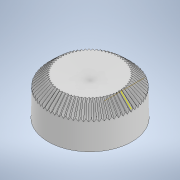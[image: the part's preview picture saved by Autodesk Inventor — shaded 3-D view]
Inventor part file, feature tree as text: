
AUTODESK INVENTOR PART (.ipt)
format: ipt  version: 2022 (Build 260153000, 153)  size: 1,119,232 bytes
history: native  units: mm
features: sketch x5, extrude x3, revolve x1, plane x1, pattern_circular x1, shell x1, fillet x1, projected_geometry x1
ambient origin geometry x8: Origin, YZ Plane, XZ Plane, XY Plane, X Axis, Y Axis, Z Axis, Center Point
bodies: Solid1 (feature_tree)
feature tree (14):
  revolve  "Revolution1"  [1 undecoded]
  sketch  "Sketch3"  dims[d2=30.79375mm d3=22.503125mm]
  plane  "Work Plane1"
  extrude  "Extrusion1"  Depth=22.503125mm
  pattern_circular  "Circular Pattern1"  [2 undecoded]
  shell  "Shell1"  Thickness=90.0deg
  extrude  "Extrusion2"  TaperAngle=0.0deg  [1 undecoded]
  extrude  "Extrusion3"  Depth=700.0mm TaperAngle=360.0deg
  fillet  "Fillet1"  Radius=1.0mm
  sketch  "Sketch2"  dims[d0=33.63625mm d1=33.1625mm]
  sketch  "Sketch4"  dims[d4=24.871875mm]
  projected_geometry  "Projected Loop1"
  sketch  "Sketch5"  dims[d5=5.448125mm]
  sketch  "Sketch6"  dims[d6=90.0deg d7=2.8425mm d8=90.0deg d9=0.0mm d10=0.0mm d11=700.0mm d12=360.0deg d14=1.0mm d15=3.0mm d16=20.0mm d17=3.0mm d18=10.0mm d19=0.0mm d20=60.0mm d22=360.0deg d24=6.0mm d25=15.0mm d26=0.0mm d27=5.0mm]
note: 4 required parameter values undecoded (feature->parameter linkage not recoverable at this tier; creation-order binding heuristic only, values carry confidence <= 0.55)